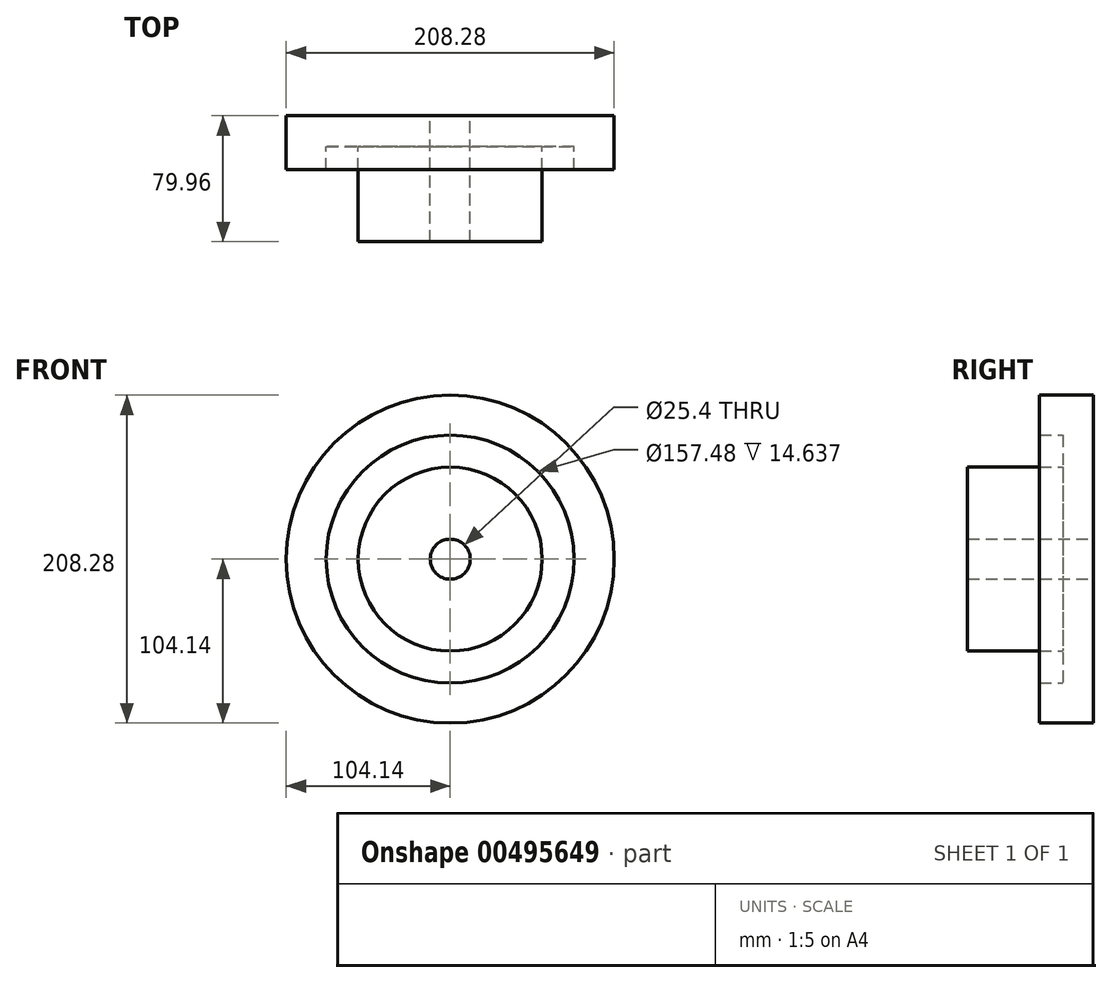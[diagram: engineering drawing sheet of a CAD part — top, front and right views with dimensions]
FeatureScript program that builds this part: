
annotation { "Feature Type Name" : "Feature", "Feature Type Description" : "" }
export const myFeature = defineFeature(function(context is Context, id is Id, definition is map)
    precondition{}
    {
        {
            var Q0;
            Q0=qCreatedBy(makeId("Right.planeOp"),FACE);
            var sketch = newSketch(context, id + "F0", { "sketchPlane" : qUnion([Q0])});
            skLineSegment(sketch, "E0", {"start": v(0, 0) * mm, "end": v(-66.08, 0) * mm});
            skLineSegment(sketch, "E1.bottom", {"start": v(0, 12.7) * mm, "end": v(-45.42, 12.7) * mm});
            skLineSegment(sketch, "E1.top", {"start": v(0, 58.42) * mm, "end": v(-45.42, 58.42) * mm});
            skLineSegment(sketch, "E1.left", {"start": v(0, 12.7) * mm, "end": v(0, 58.42) * mm});
            skLineSegment(sketch, "E1.right", {"start": v(-45.42, 12.7) * mm, "end": v(-45.42, 58.42) * mm});
            skLineSegment(sketch, "E2.bottom", {"start": v(0, 12.7) * mm, "end": v(-19.59, 12.7) * mm});
            skLineSegment(sketch, "E2.top", {"start": v(0, 78.74) * mm, "end": v(-19.59, 78.74) * mm});
            skLineSegment(sketch, "E2.left", {"start": v(0, 12.7) * mm, "end": v(0, 78.74) * mm});
            skLineSegment(sketch, "E2.right", {"start": v(-19.59, 12.7) * mm, "end": v(-19.59, 78.74) * mm});
            skLineSegment(sketch, "E3.bottom", {"start": v(0, 78.74) * mm, "end": v(-34.23, 78.74) * mm});
            skLineSegment(sketch, "E3.top", {"start": v(0, 104.14) * mm, "end": v(-34.23, 104.14) * mm});
            skLineSegment(sketch, "E3.left", {"start": v(0, 78.74) * mm, "end": v(0, 104.14) * mm});
            skLineSegment(sketch, "E3.right", {"start": v(-34.23, 78.74) * mm, "end": v(-34.23, 104.14) * mm});
            skLineSegment(sketch, "E4.MirrorCS", {"start": v(0, -12.7) * mm, "end": v(0, -58.42) * mm});
            skLineSegment(sketch, "E5.MirrorCS", {"start": v(0, -78.74) * mm, "end": v(-19.59, -78.74) * mm});
            skLineSegment(sketch, "E6.MirrorCS", {"start": v(-34.23, -78.74) * mm, "end": v(-34.23, -104.14) * mm});
            skLineSegment(sketch, "E7.MirrorCS", {"start": v(0, -78.74) * mm, "end": v(0, -104.14) * mm});
            skLineSegment(sketch, "E8.MirrorCS", {"start": v(0, -104.14) * mm, "end": v(-34.23, -104.14) * mm});
            skLineSegment(sketch, "E9.MirrorCS", {"start": v(0, -12.7) * mm, "end": v(-45.42, -12.7) * mm});
            skLineSegment(sketch, "E10.MirrorCS", {"start": v(0, -58.42) * mm, "end": v(-45.42, -58.42) * mm});
            skLineSegment(sketch, "E11.MirrorCS", {"start": v(-45.42, -12.7) * mm, "end": v(-45.42, -58.42) * mm});
            skLineSegment(sketch, "E12.MirrorCS", {"start": v(0, -78.74) * mm, "end": v(-34.23, -78.74) * mm});
            skLineSegment(sketch, "E13.MirrorCS", {"start": v(-19.59, -12.7) * mm, "end": v(-19.59, -78.74) * mm});
            skLineSegment(sketch, "E14.MirrorCS", {"start": v(0, -12.7) * mm, "end": v(-19.59, -12.7) * mm});
            skLineSegment(sketch, "E15.MirrorCS", {"start": v(0, -12.7) * mm, "end": v(0, -78.74) * mm});
            skSolve(sketch);
        }
        {
            var Q0;
            {var subQ3=sQuery(id+"F0.wireOp",EDGE,"E6.MirrorCS");Q0=makeQuery(id+"F0.imprint","IMPRINT",FACE,{"disambiguationData":[TD([[makeQuery(id+"F0.imprint","IMPRINT",EDGE,{"derivedFrom":subQ3}),1.0]])]});}
            var Q1;
            {var subQ0=sQuery(id+"F0.wireOp",EDGE,"E9.MirrorCS");Q1=makeQuery(id+"F0.imprint","IMPRINT",FACE,{"disambiguationData":[TD([[makeQuery(id+"F0.imprint","IMPRINT",EDGE,{"derivedFrom":subQ0}),1.0]])]});}
            var Q2;
            {var subQ0=sQuery(id+"F0.wireOp",EDGE,"E15.MirrorCS");var subQ1=sQuery(id+"F0.wireOp",EDGE,"E10.MirrorCS");var subQ2=makeQuery(id+"F0.imprint","INTERSECT",VERTEX,{"derivedFrom":[subQ1,subQ0]});Q2=makeQuery(id+"F0.imprint","IMPRINT",FACE,{"disambiguationData":[TD([[makeQuery(id+"F0.imprint","IMPRINT",EDGE,{"disambiguationData":[TD([[subQ2,-1.0]])],"derivedFrom":subQ1}),1.0]])]});}
            var Q3;
            {var subQ5=sQuery(id+"F0.wireOp",EDGE,"E14.MirrorCS");Q3=makeQuery(id+"F0.imprint","IMPRINT",FACE,{"disambiguationData":[TD([[makeQuery(id+"F0.imprint","IMPRINT",EDGE,{"derivedFrom":subQ5}),1.0]])]});}
            var Q4;
            Q4=sQuery(id+"F0.wireOp",EDGE,"E0");
            revolve(context, id + "F1", {"entities" : qUnion([Q0, Q1, Q2, Q3]), "axis" : qUnion([Q4]), "revolveType" : RevolveType.FULL});
        }
        {
            var Q0;
            Q0=makeQuery(id+"F1.opRevolve","SWEPT_FACE",FACE,{"disambiguationData":[OSD([sQuery(id+"F0.wireOp",EDGE,"E11.MirrorCS")])]});
            extrude(context, id + "F2", {"entities" : qUnion([Q0]), "operationType" : NewBodyOperationType.ADD, "depth" : 34.54 * mm});
        }
    });
